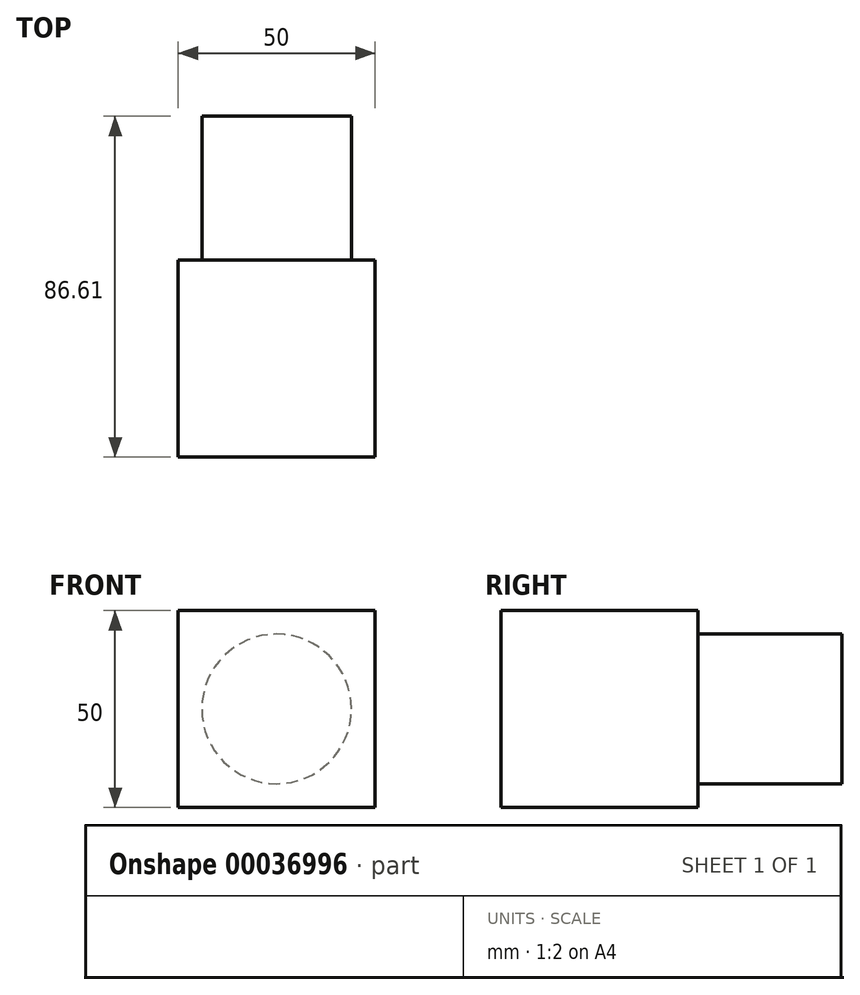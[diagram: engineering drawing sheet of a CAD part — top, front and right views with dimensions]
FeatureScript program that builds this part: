
annotation { "Feature Type Name" : "Feature", "Feature Type Description" : "" }
export const myFeature = defineFeature(function(context is Context, id is Id, definition is map)
    precondition{}
    {
        {
            var Q0;
            Q0=qCreatedBy(makeId("Front.planeOp"),FACE);
            var sketch = newSketch(context, id + "F0", { "sketchPlane" : qUnion([Q0])});
            skLineSegment(sketch, "E0.bottom", {"start": v(0, 50) * mm, "end": v(50, 50) * mm});
            skLineSegment(sketch, "E0.top", {"start": v(0, 0) * mm, "end": v(50, 0) * mm});
            skLineSegment(sketch, "E0.left", {"start": v(0, 50) * mm, "end": v(0, 0) * mm});
            skLineSegment(sketch, "E0.right", {"start": v(50, 50) * mm, "end": v(50, 0) * mm});
            skSolve(sketch);
        }
        {
            var Q0;
            Q0 = qSketchRegion(id + "F0", true);
            extrude(context, id + "F1", {"entities" : qUnion([Q0]), "depth" : 50 * mm});
        }
        {
            var Q0;
            Q0=makeQuery(id+"F1.opExtrude","CAP_FACE",FACE,{"disambiguationData":[OSD([sQuery(id+"F0.wireOp",EDGE,"E0.bottom"),sQuery(id+"F0.wireOp",EDGE,"E0.top"),sQuery(id+"F0.wireOp",EDGE,"E0.left"),sQuery(id+"F0.wireOp",EDGE,"E0.right")])],"isStart":false});
            var sketch = newSketch(context, id + "F2", { "sketchPlane" : qUnion([Q0])});
            skCircle(sketch, "E1", {"center": v(25, 25) * mm, "radius": 19 * mm});
            skSolve(sketch);
        }
        {
            var Q0;
            Q0 = qSketchRegion(id + "F2", true);
            extrude(context, id + "F3", {"entities" : qUnion([Q0]), "operationType" : NewBodyOperationType.ADD, "endBound" : BoundingType.THROUGH_ALL, "oppositeDirection" : true, "depth" : 25.4 * mm});
        }
    });
